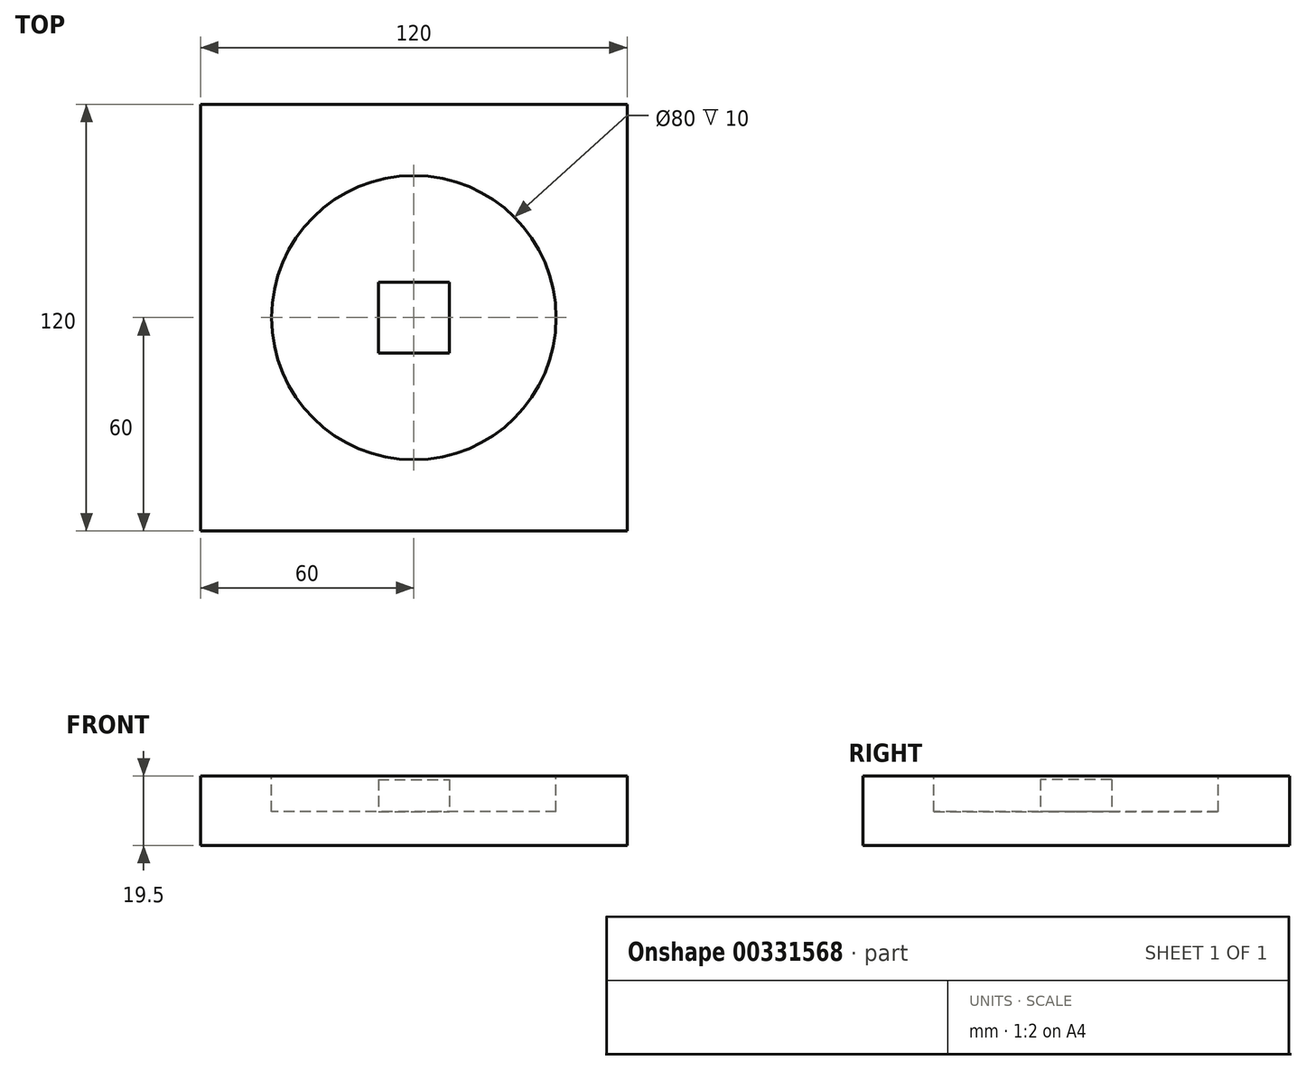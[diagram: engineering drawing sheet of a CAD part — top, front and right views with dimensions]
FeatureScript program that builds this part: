
annotation { "Feature Type Name" : "Feature", "Feature Type Description" : "" }
export const myFeature = defineFeature(function(context is Context, id is Id, definition is map)
    precondition{}
    {
        {
            var Q0;
            Q0=qCreatedBy(makeId("Top.planeOp"),FACE);
            var sketch = newSketch(context, id + "F0", { "sketchPlane" : qUnion([Q0])});
            skLineSegment(sketch, "E0.bottom", {"start": v(0, 0) * mm, "end": v(120, 0) * mm});
            skLineSegment(sketch, "E0.top", {"start": v(0, 120) * mm, "end": v(120, 120) * mm});
            skLineSegment(sketch, "E0.left", {"start": v(0, 0) * mm, "end": v(0, 120) * mm});
            skLineSegment(sketch, "E0.right", {"start": v(120, 0) * mm, "end": v(120, 120) * mm});
            skSolve(sketch);
        }
        {
            var Q0;
            Q0=makeQuery(id+"F0.imprint","IMPRINT",FACE,{"disambiguationData":[TD([[makeQuery(id+"F0.imprint","IMPRINT",EDGE,{"derivedFrom":sQuery(id+"F0.wireOp",EDGE,"E0.bottom")}),1.0]])]});
            extrude(context, id + "F1", {"entities" : qUnion([Q0]), "depth" : 19.5 * mm});
        }
        {
            var Q0;
            Q0=makeQuery(id+"F1.opExtrude","CAP_FACE",FACE,{"disambiguationData":[OSD([sQuery(id+"F0.wireOp",EDGE,"E0.bottom"),sQuery(id+"F0.wireOp",EDGE,"E0.top"),sQuery(id+"F0.wireOp",EDGE,"E0.left"),sQuery(id+"F0.wireOp",EDGE,"E0.right")])],"isStart":false});
            var sketch = newSketch(context, id + "F2", { "sketchPlane" : qUnion([Q0])});
            skCircle(sketch, "E1", {"center": v(60, 60) * mm, "radius": 40 * mm});
            skSolve(sketch);
        }
        {
            var Q0;
            Q0 = qSketchRegion(id + "F2", true);
            extrude(context, id + "F3", {"entities" : qUnion([Q0]), "operationType" : NewBodyOperationType.REMOVE, "oppositeDirection" : true, "depth" : 10 * mm});
        }
        {
            var Q0;
            Q0=makeQuery(id+"F3.boolean.opBoolean","COPY",FACE,{"derivedFrom":makeQuery(id+"F3.opExtrude","CAP_FACE",FACE,{"disambiguationData":[OSD([sQuery(id+"F2.wireOp",EDGE,"E1")])],"isStart":false})});
            var sketch = newSketch(context, id + "F4", { "sketchPlane" : qUnion([Q0])});
            skLineSegment(sketch, "E2.bottom", {"start": v(50, 70) * mm, "end": v(70, 70) * mm});
            skLineSegment(sketch, "E2.top", {"start": v(50, 50) * mm, "end": v(70, 50) * mm});
            skLineSegment(sketch, "E2.left", {"start": v(50, 70) * mm, "end": v(50, 50) * mm});
            skLineSegment(sketch, "E2.right", {"start": v(70, 70) * mm, "end": v(70, 50) * mm});
            skSolve(sketch);
        }
        {
            var Q0;
            Q0=makeQuery(id+"F4.imprint","IMPRINT",FACE,{"disambiguationData":[TD([[makeQuery(id+"F4.imprint","IMPRINT",EDGE,{"derivedFrom":sQuery(id+"F4.wireOp",EDGE,"E2.bottom")}),-1.0]])]});
            var sketch = newSketch(context, id + "F5", { "sketchPlane" : qUnion([Q0])});
            skSolve(sketch);
        }
        {
            var Q0;
            Q0 = qSketchRegion(id + "F5", true);
            var Q1;
            Q1 = qSketchRegion(id + "F4", true);
            extrude(context, id + "F6", {"entities" : qUnion([Q0, Q1]), "operationType" : NewBodyOperationType.ADD, "depth" : 9 * mm});
        }
    });
